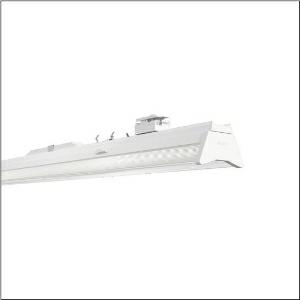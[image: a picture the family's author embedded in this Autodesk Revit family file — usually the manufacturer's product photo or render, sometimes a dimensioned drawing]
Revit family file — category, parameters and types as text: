
# Revit family: licross_r__21_performance_ho_52td16dn4e5m_0710
name_source: partatom
category: Lighting Fixtures
units: mm (PartAtom-declared; Revit-internal decimal feet)

## family parameters
Cut with Voids When Loaded = No
Host = Face
Light Source = No
Part Type = Normal
Room Calculation Point = No
Round Connector Dimension = Use Diameter
Shared = No

## types (1)
- --- (1 x LED, 14870 lm, 84.9 W, 4000K)
    Apparent Load = 85 VA
    CIE Flux Codes = 63 87 95 78 100
    Color Rendering = 80
    Color Temperature = 4000K
    Default Elevation = 1800 mm
    Description = Licross® 21 Performance HO, luminaire insert, of sheet steel, galvanised, coil coated, white, length: 1.500mm, width: 120mm, height: 123mm, LED rated luminous flux: 14.870lm, light colour: 840, control gear: DALI 2, with plug, 5-pole, with phase selection, mains connection: 220..240V, AC, 50/60Hz, rated input power: 85W, halogen-free wiring, primary light control with lens, of plastic, primary optical cover: cover, of PMMA, light emission: direct/indirect distribution, primary light characteristic: symmetric, protection rating (complete): IP54, insulation class (complete): insulation class I (protective earthing), certification: CE, ENEC, VDE, UKCA, protection symbol: D if used in an environment with non-conductive dust loads with corresponding accessories, impact resistance: IK06, permissible ambient temperature for indoor applications: -25..+35°C, corresponds to IFS (International Featured Standards) requirements for safety and quality in the food industry, reducing of maximum allowable ambient temperature of 5°C with ceiling mounting, LABS conformity tested according to VDMA 24364:2018-05, packaging unit: 1 piece
    Height = 114 mm
    Lamp = 1 x LED
    Lamp Light Flux = 14870 lm
    Lamp Power = 84.9 W
    Lamp count = 1
    Length = 1500 mm
    Luminous efficacy = 175 lm/W
    Manufacturer = Siteco
    ModVariant = No
    Model = 52TD16DN4E5M
    Mounting Place = Ceiling
    Mounting Type = Pendant
    Number of Poles = 1
    OnlyDefault = Yes
    Power Factor = 1
    Product Name = Licross® 21 Performance HO
    Product group = luminaire insert
    ProductGroupID = 902
    Protection Class = Protection class I
    Protection Degree = IP 54
    RLX_Detail_Level = 1
    RLX_Emergency_Light_Flux = 0 lm
    RLX_Emergency_Type = 0
    RLX_Emergency_Type_DB = No
    RlxData = <blob elided: 33977 chars, md5=904c459d>
    Socket = socket
    Standby Power = 0 W
    System Light Flux = 14870 lm
    System Power = 85 W
    Type Comments = factory setting: luminous flux: 100 % | dim-lin: 254 | 484 mA
    Type Image = l_1256138.jpg
    URL = http://relux.com
    VarID = @adj_129306
    Voltage = 0 V
    Weight = 0.00 kg
    Width = 120 mm

## geometry (parser evidence)
native form markers: Blend x4, Sweep x13
no freeform markers — native parametric forms only
